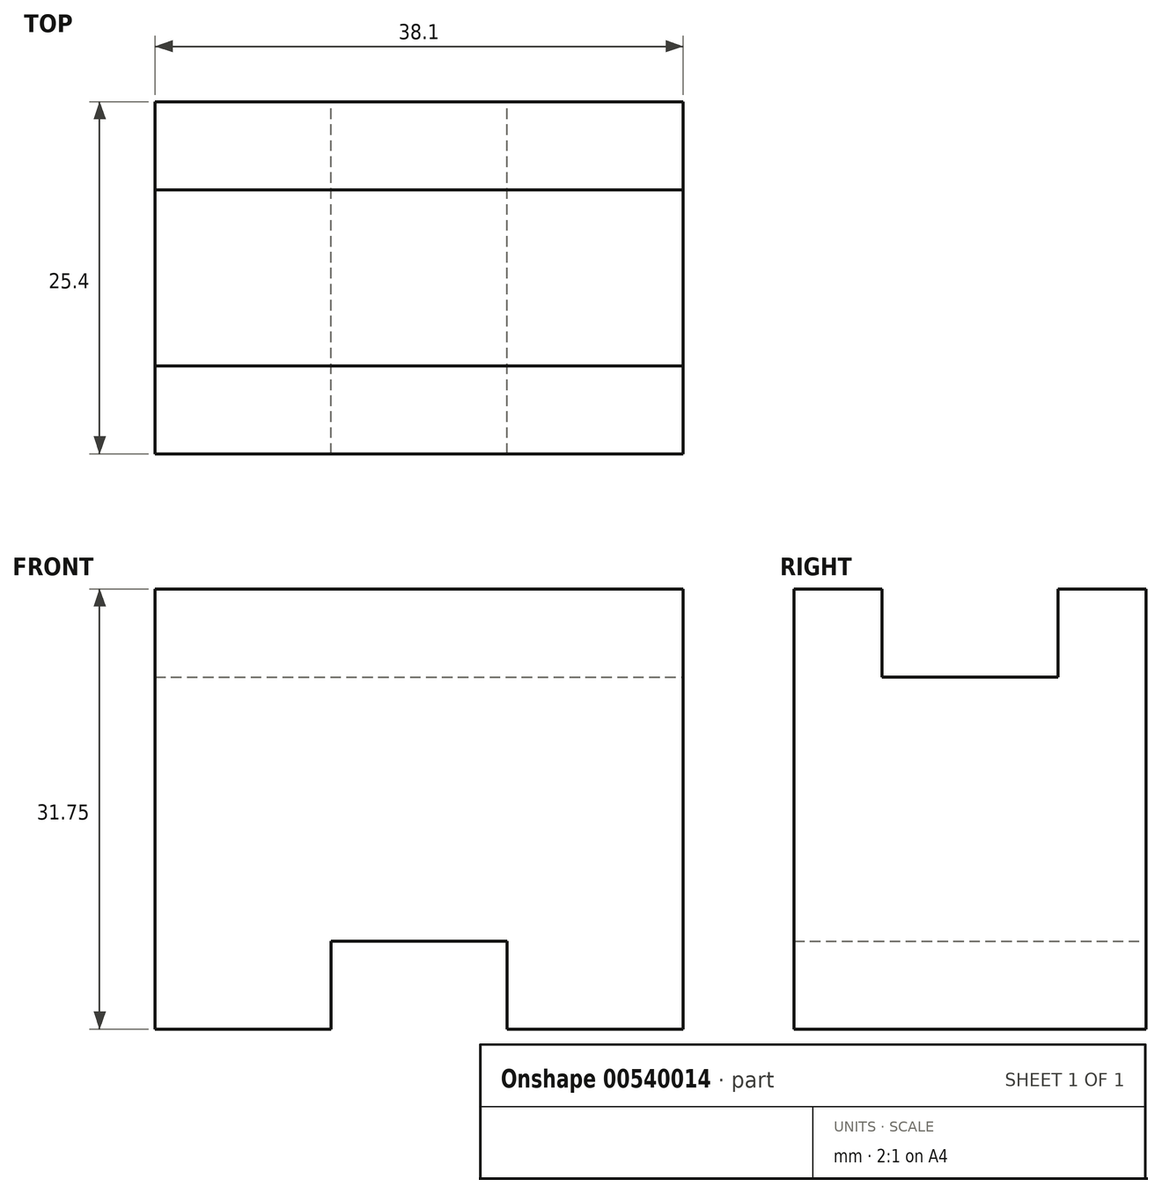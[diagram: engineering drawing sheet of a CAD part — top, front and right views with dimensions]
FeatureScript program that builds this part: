
annotation { "Feature Type Name" : "Feature", "Feature Type Description" : "" }
export const myFeature = defineFeature(function(context is Context, id is Id, definition is map)
    precondition{}
    {
        {
            var Q0;
            Q0=qCreatedBy(makeId("Front.planeOp"),FACE);
            var sketch = newSketch(context, id + "F0", { "sketchPlane" : qUnion([Q0])});
            skLineSegment(sketch, "E0", {"start": v(0, 0) * mm, "end": v(0, 6.35) * mm});
            skLineSegment(sketch, "E1", {"start": v(0, 6.35) * mm, "end": v(12.7, 6.35) * mm});
            skLineSegment(sketch, "E2", {"start": v(12.7, 6.35) * mm, "end": v(12.7, 0) * mm});
            skLineSegment(sketch, "E3", {"start": v(12.7, 0) * mm, "end": v(25.4, 0) * mm});
            skLineSegment(sketch, "E4", {"start": v(0, 0) * mm, "end": v(-12.7, 0) * mm});
            skLineSegment(sketch, "E5", {"start": v(-12.7, 0) * mm, "end": v(-12.7, 31.75) * mm});
            skLineSegment(sketch, "E6", {"start": v(-12.7, 31.75) * mm, "end": v(25.4, 31.75) * mm});
            skLineSegment(sketch, "E7", {"start": v(25.4, 31.75) * mm, "end": v(25.4, 0) * mm});
            skSolve(sketch);
        }
        {
            var Q0;
            Q0 = qSketchRegion(id + "F0", true);
            extrude(context, id + "F1", {"entities" : qUnion([Q0]), "depth" : 25.4 * mm, "offsetDistance" : 25.4 * mm});
        }
        {
            var Q0;
            Q0=makeQuery(id+"F1.opExtrude","SWEPT_FACE",FACE,{"disambiguationData":[OSD([sQuery(id+"F0.wireOp",EDGE,"E6")])]});
            var sketch = newSketch(context, id + "F2", { "sketchPlane" : qUnion([Q0])});
            skLineSegment(sketch, "E8", {"start": v(-12.7, 0) * mm, "end": v(-12.7, -6.35) * mm});
            skLineSegment(sketch, "E9", {"start": v(-12.7, -6.35) * mm, "end": v(-12.7, -19.05) * mm});
            skLineSegment(sketch, "E10", {"start": v(-12.7, -19.05) * mm, "end": v(-12.7, -25.4) * mm});
            skLineSegment(sketch, "E11", {"start": v(-12.7, -6.35) * mm, "end": v(25.4, -6.35) * mm});
            skLineSegment(sketch, "E12", {"start": v(25.4, -6.35) * mm, "end": v(25.4, -19.05) * mm});
            skLineSegment(sketch, "E13", {"start": v(25.4, -19.05) * mm, "end": v(-12.7, -19.05) * mm});
            skSolve(sketch);
        }
        {
            var Q0;
            Q0=makeQuery(id+"F2.imprint","IMPRINT",FACE,{"disambiguationData":[TD([[makeQuery(id+"F2.imprint","IMPRINT",EDGE,{"derivedFrom":sQuery(id+"F2.wireOp",EDGE,"E9")}),-1.0]])]});
            extrude(context, id + "F3", {"entities" : qUnion([Q0]), "operationType" : NewBodyOperationType.REMOVE, "oppositeDirection" : true, "depth" : 6.35 * mm, "offsetDistance" : 25.4 * mm});
        }
    });
